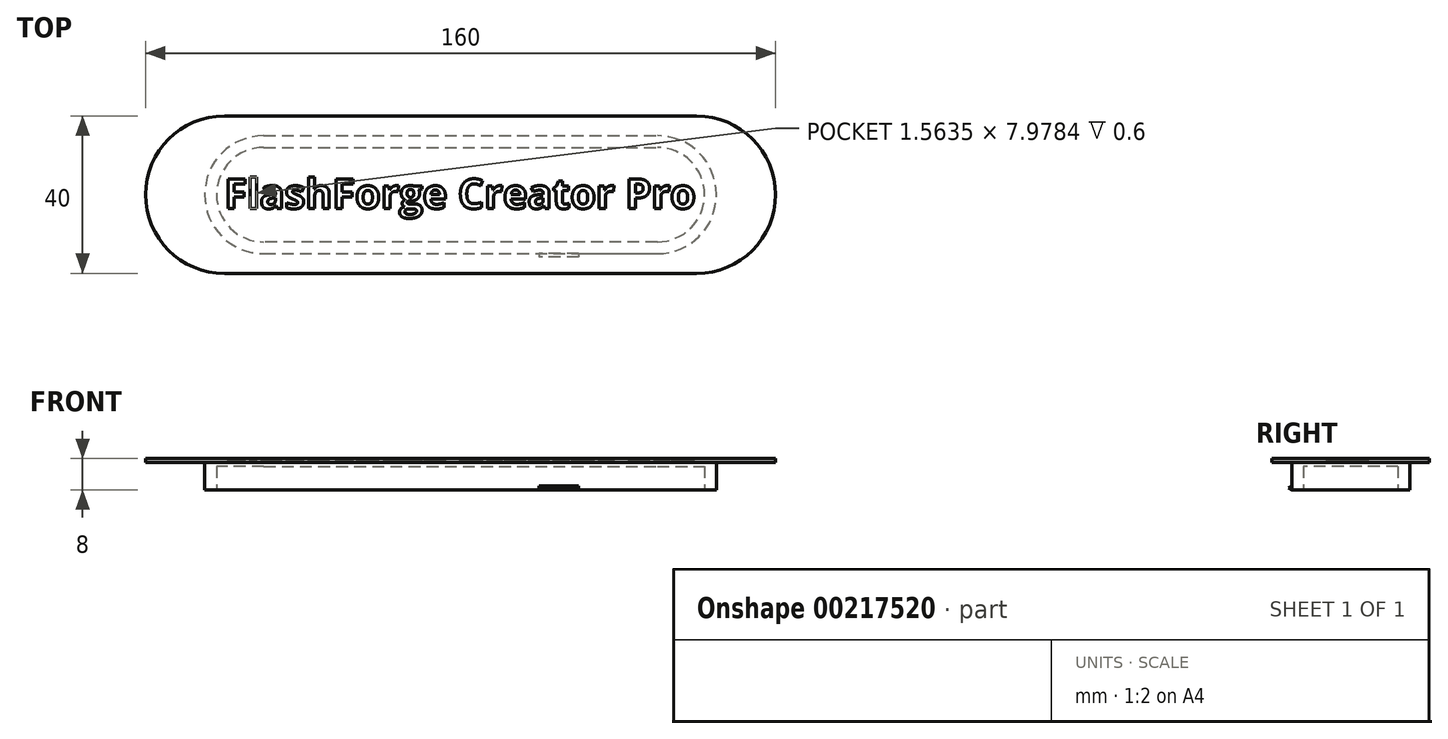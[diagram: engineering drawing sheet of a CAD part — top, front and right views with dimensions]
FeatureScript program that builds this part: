
annotation { "Feature Type Name" : "Feature", "Feature Type Description" : "" }
export const myFeature = defineFeature(function(context is Context, id is Id, definition is map)
    precondition{}
    {
        {
            var Q0;
            Q0=qCreatedBy(makeId("Top.planeOp"),FACE);
            var sketch = newSketch(context, id + "F0", { "sketchPlane" : qUnion([Q0])});
            skLineSegment(sketch, "E0.bottom", {"start": v(-60, 20) * mm, "end": v(60, 20) * mm});
            skLineSegment(sketch, "E0.top", {"start": v(-60, -20) * mm, "end": v(60, -20) * mm});
            skLineSegment(sketch, "E0.left", {"start": v(-60, 20) * mm, "end": v(-60, -20) * mm});
            skLineSegment(sketch, "E0.right", {"start": v(60, 20) * mm, "end": v(60, -20) * mm});
            skArc(sketch, "E1", {"start": v(-60, 20) * mm, "mid": v(-80, 0) * mm, "end": v(-60, -20) * mm});
            skArc(sketch, "E2", {"start": v(60, -20) * mm, "mid": v(80, 0) * mm, "end": v(60, 20) * mm});
            skPoint(sketch, "E3", {"position": v(-80, 0) * mm});
            skPoint(sketch, "E4", {"position": v(80, 0) * mm});
            skSolve(sketch);
        }
        {
            var Q0;
            Q0 = qSketchRegion(id + "F0", true);
            extrude(context, id + "F1", {"entities" : qUnion([Q0]), "depth" : 1 * mm});
        }
        {
            var Q0;
            Q0=makeQuery(id+"F1.opExtrude","CAP_FACE",FACE,{"disambiguationData":[OSD([sQuery(id+"F0.wireOp",EDGE,"E0.bottom"),sQuery(id+"F0.wireOp",EDGE,"E0.top"),sQuery(id+"F0.wireOp",EDGE,"E1"),sQuery(id+"F0.wireOp",EDGE,"E2")])],"isStart":true});
            var sketch = newSketch(context, id + "F2", { "sketchPlane" : qUnion([Q0])});
            skLineSegment(sketch, "E5.bottom", {"start": v(-50, 15) * mm, "end": v(50, 15) * mm});
            skLineSegment(sketch, "E5.top", {"start": v(-50, -15) * mm, "end": v(50, -15) * mm});
            skLineSegment(sketch, "E5.left", {"start": v(-50, 15) * mm, "end": v(-50, -15) * mm});
            skLineSegment(sketch, "E5.right", {"start": v(50, 15) * mm, "end": v(50, -15) * mm});
            skArc(sketch, "E6", {"start": v(-50, 15) * mm, "mid": v(-65, 0) * mm, "end": v(-50, -15) * mm});
            skArc(sketch, "E7", {"start": v(50, -15) * mm, "mid": v(65, 0) * mm, "end": v(50, 15) * mm});
            skSolve(sketch);
        }
        {
            var Q0;
            Q0 = qSketchRegion(id + "F2", true);
            extrude(context, id + "F3", {"entities" : qUnion([Q0]), "operationType" : NewBodyOperationType.ADD, "depth" : 7 * mm});
        }
        {
            var Q0;
            Q0=qCreatedBy(makeId("Right.planeOp"),FACE);
            cPlane(context, id + "F4", {"entities" : qUnion([Q0]), "cplaneType" : CPlaneType.OFFSET, "offset" : 25 * mm, "width" : 150 * mm, "height" : 150 * mm});
        }
        {
            var Q0;
            Q0=qCreatedBy(id+"F4.planeOp",FACE);
            var sketch = newSketch(context, id + "F5", { "sketchPlane" : qUnion([Q0])});
            skLineSegment(sketch, "E8.0", {"start": v(-15, -7) * mm, "end": v(-15, 0) * mm, "construction": true});
            skLineSegment(sketch, "E9.0", {"start": v(-20, 0) * mm, "end": v(20, 0) * mm, "construction": true});
            skCircle(sketch, "E10.cCircle", {"center": v(-15.29, -6.5) * mm, "radius": 0.29 * mm, "construction": true});
            skLineSegment(sketch, "E10.0", {"start": v(-15, -7) * mm, "end": v(-15.87, -6.5) * mm});
            skLineSegment(sketch, "E10.1", {"start": v(-15.87, -6.5) * mm, "end": v(-15, -6) * mm});
            skLineSegment(sketch, "E10.2", {"start": v(-15, -6) * mm, "end": v(-15, -7) * mm});
            skPoint(sketch, "E10.0.midPoint", {"position": v(-15.43, -6.75) * mm});
            skSolve(sketch);
        }
        {
            var Q0;
            Q0 = qSketchRegion(id + "F5", true);
            extrude(context, id + "F6", {"entities" : qUnion([Q0]), "operationType" : NewBodyOperationType.ADD, "depth" : 5 * mm, "hasSecondDirection" : true, "secondDirectionOppositeDirection" : true, "secondDirectionDepth" : 5 * mm});
        }
        {
            var Q0;
            Q0=makeQuery(id+"F3.opExtrude","CAP_FACE",FACE,{"disambiguationData":[OSD([sQuery(id+"F2.wireOp",EDGE,"E5.bottom"),sQuery(id+"F2.wireOp",EDGE,"E5.top"),sQuery(id+"F2.wireOp",EDGE,"E6"),sQuery(id+"F2.wireOp",EDGE,"E7")])],"isStart":false});
            var sketch = newSketch(context, id + "F7", { "sketchPlane" : qUnion([Q0])});
            skLineSegment(sketch, "E11.0", {"start": v(-30, 12) * mm, "end": v(-50, 12) * mm});
            skLineSegment(sketch, "E11.1", {"start": v(20, -12) * mm, "end": v(30, -12) * mm});
            skLineSegment(sketch, "E11.2", {"start": v(-20, -12) * mm, "end": v(20, -12) * mm});
            skLineSegment(sketch, "E11.3", {"start": v(-30, -12) * mm, "end": v(-20, -12) * mm});
            skLineSegment(sketch, "E11.4", {"start": v(-50, -12) * mm, "end": v(-30, -12) * mm});
            skLineSegment(sketch, "E11.5", {"start": v(30, -12) * mm, "end": v(50, -12) * mm});
            skArc(sketch, "E11.6", {"start": v(-50, 12) * mm, "mid": v(-62, 0) * mm, "end": v(-50, -12) * mm});
            skArc(sketch, "E11.7", {"start": v(50, -12) * mm, "mid": v(62, 0) * mm, "end": v(50, 12) * mm});
            skLineSegment(sketch, "E11.8", {"start": v(50, 12) * mm, "end": v(30, 12) * mm});
            skLineSegment(sketch, "E11.9", {"start": v(30, 12) * mm, "end": v(20, 12) * mm});
            skLineSegment(sketch, "E11.10", {"start": v(20, 12) * mm, "end": v(-20, 12) * mm});
            skLineSegment(sketch, "E11.11", {"start": v(-20, 12) * mm, "end": v(-30, 12) * mm});
            skSolve(sketch);
        }
        {
            var Q0;
            Q0 = qSketchRegion(id + "F7", true);
            var Q1;
            Q1=makeQuery(id+"F1.opExtrude","CAP_FACE",FACE,{"disambiguationData":[OSD([sQuery(id+"F0.wireOp",EDGE,"E0.bottom"),sQuery(id+"F0.wireOp",EDGE,"E0.top"),sQuery(id+"F0.wireOp",EDGE,"E1"),sQuery(id+"F0.wireOp",EDGE,"E2")])],"isStart":true});
            extrude(context, id + "F8", {"entities" : qUnion([Q0]), "operationType" : NewBodyOperationType.REMOVE, "oppositeDirection" : true, "endBoundEntityFace" : qUnion([Q1]), "depth" : 6 * mm});
        }
        {
            var Q0;
            Q0=makeQuery(id+"F1.opExtrude","CAP_FACE",FACE,{"disambiguationData":[OSD([sQuery(id+"F0.wireOp",EDGE,"E0.bottom"),sQuery(id+"F0.wireOp",EDGE,"E0.top"),sQuery(id+"F0.wireOp",EDGE,"E1"),sQuery(id+"F0.wireOp",EDGE,"E2")])],"isStart":false});
            var sketch = newSketch(context, id + "F9", { "sketchPlane" : qUnion([Q0])});
            skText(sketch, "E12", { "text": "FlashForge Creator Pro", "fontName": "OpenSans-Bold.ttf"});
            const initialGuessF9  = {"E12": [-0.06, -0.00352, 1, 0, 0.00756]};
            skSetInitialGuess(sketch, initialGuessF9);
            skSolve(sketch);
        }
        {
            var Q0;
            Q0 = qSketchRegion(id + "F9", true);
            extrude(context, id + "F10", {"entities" : qUnion([Q0]), "operationType" : NewBodyOperationType.REMOVE, "oppositeDirection" : true, "depth" : .6 * mm});
        }
    });
